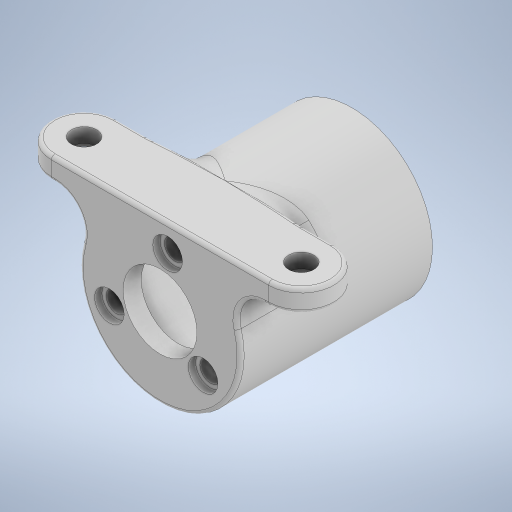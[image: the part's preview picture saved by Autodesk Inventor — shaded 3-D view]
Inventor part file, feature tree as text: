
AUTODESK INVENTOR PART (.ipt)
format: ipt  version: 2024.2 (Build 282272000, 272)  size: 424,448 bytes
history: native  units: mm
features: sketch x7, extrude x5, hole x2, fillet x2, plane x1, chamfer x1
ambient origin geometry x8: Origin, YZ Plane, XZ Plane, XY Plane, X Axis, Y Axis, Z Axis, Center Point
bodies: Solid1 (feature_tree)
feature tree (18):
  extrude  "Extrusion1"  Depth=2.9mm
  extrude  "Extrusion2"  Depth=30.0mm TaperAngle=360.0deg
  extrude  "Extrusion3"  Depth=22.25mm
  plane  "Work Plane1"
  extrude  "Extrusion4"  Depth=4.1mm
  extrude  "Extrusion5"  Depth=20.25mm
  hole  "Hole1"  [1 undecoded]
  hole  "Hole2"  [1 undecoded]
  fillet  "Fillet1"  Radius=15.0mm
  fillet  "Fillet2"  Radius=3.0mm
  chamfer  "Chamfer1"  Distance=1.5mm
  sketch  "Sketch1"  dims[d0=10.2mm d1=2.9mm]
  sketch  "Sketch2"  dims[d2=7.55mm d3=30.0mm d5=360.0deg]
  sketch  "Sketch3"  dims[d7=1.396263mm d8=22.25mm]
  sketch  "Sketch4"  dims[d9=1.5mm d10=0.0mm d11=4.1mm]
  sketch  "Sketch5"  dims[d12=1.0mm d13=0.0mm d14=20.25mm]
  sketch  "Sketch6"  dims[d15=24.0mm d16=0.0mm d17=11.125mm]
  sketch  "Sketch7"  dims[d18=9.0mm d19=30.0mm d20=15.0mm d21=3.0mm d22=0.0mm d23=1.5mm d24=0.0mm d25=2.9mm d26=6.0mm d27=4.1mm d28=1.0mm d29=90.0deg d30=8.0mm d31=20.594885mm d32=3.5mm d33=6.0mm d34=5.25mm d35=1.0mm d36=90.0deg d37=8.0mm d38=20.594885mm d39=4.0mm d40=0.5mm d41=0.5mm d42=2.0mm d43=45.0deg]
note: 2 required parameter values undecoded (feature->parameter linkage not recoverable at this tier; creation-order binding heuristic only, values carry confidence <= 0.55)
